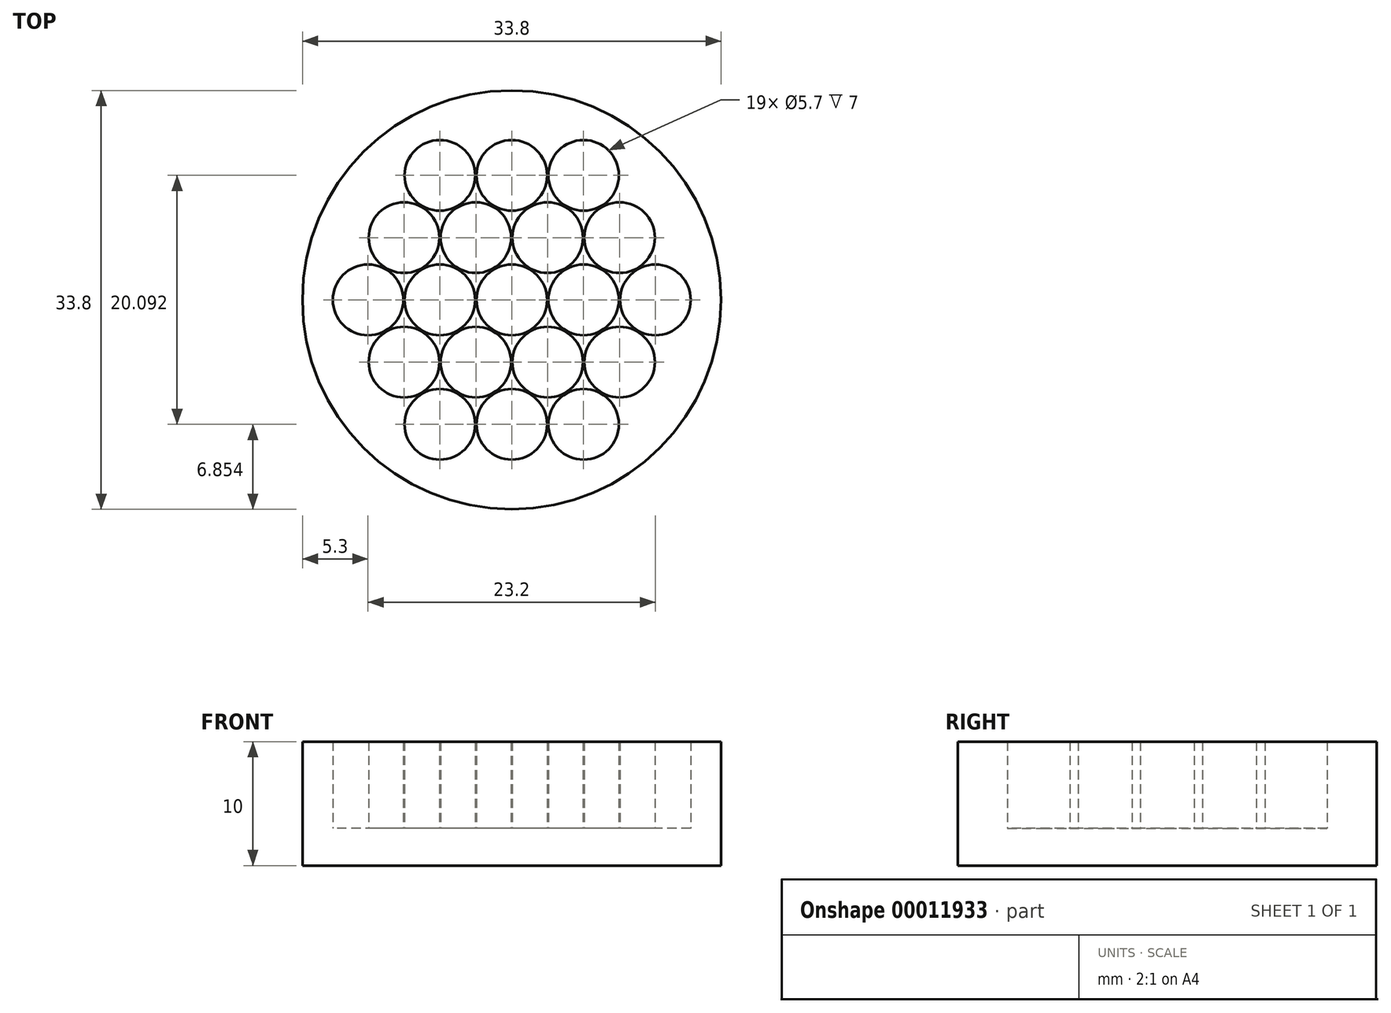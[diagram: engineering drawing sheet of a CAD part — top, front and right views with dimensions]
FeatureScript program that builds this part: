
annotation { "Feature Type Name" : "Feature", "Feature Type Description" : "" }
export const myFeature = defineFeature(function(context is Context, id is Id, definition is map)
    precondition{}
    {
        {
            var Q0;
            Q0=qCreatedBy(makeId("Top.planeOp"),FACE);
            var sketch = newSketch(context, id + "F0", { "sketchPlane" : qUnion([Q0])});
            skCircle(sketch, "E0", {"center": v(0, 0) * mm, "radius": 16.9 * mm});
            skLineSegment(sketch, "E1", {"start": v(-16.9, 0) * mm, "end": v(16.9, 0) * mm, "construction": true});
            skCircle(sketch, "E2.cCircle", {"center": v(0, 0) * mm, "radius": 16.9 * mm, "construction": true});
            skLineSegment(sketch, "E2.0", {"start": v(16.9, 0) * mm, "end": v(8.45, -14.64) * mm});
            skLineSegment(sketch, "E2.1", {"start": v(8.45, -14.64) * mm, "end": v(-8.45, -14.64) * mm});
            skLineSegment(sketch, "E2.2", {"start": v(-8.45, -14.64) * mm, "end": v(-16.9, 0) * mm});
            skLineSegment(sketch, "E2.3", {"start": v(-16.9, 0) * mm, "end": v(-8.45, 14.64) * mm});
            skLineSegment(sketch, "E2.4", {"start": v(-8.45, 14.64) * mm, "end": v(8.45, 14.64) * mm});
            skLineSegment(sketch, "E2.5", {"start": v(8.45, 14.64) * mm, "end": v(16.9, 0) * mm});
            skCircle(sketch, "E3", {"center": v(0, 0) * mm, "radius": 2.85 * mm});
            skCircle(sketch, "E4.1.0.0", {"center": v(5.8, 0) * mm, "radius": 2.85 * mm});
            skCircle(sketch, "E4.2.0.0", {"center": v(11.6, 0) * mm, "radius": 2.85 * mm});
            skLineSegment(sketch, "E4.direction1", {"start": v(0, 0) * mm, "end": v(5.8, 0) * mm, "construction": true});
            skCircle(sketch, "E5.1.0", {"center": v(2.9, 5.02) * mm, "radius": 2.85 * mm});
            skCircle(sketch, "E5.2.0", {"center": v(-2.9, 5.02) * mm, "radius": 2.85 * mm});
            skCircle(sketch, "E5.3.0", {"center": v(-5.8, 0) * mm, "radius": 2.85 * mm});
            skCircle(sketch, "E5.4.0", {"center": v(-2.9, -5.02) * mm, "radius": 2.85 * mm});
            skCircle(sketch, "E5.5.0", {"center": v(2.9, -5.02) * mm, "radius": 2.85 * mm});
            skCircle(sketch, "E6.1.0", {"center": v(5.8, 10.05) * mm, "radius": 2.85 * mm});
            skCircle(sketch, "E6.2.0", {"center": v(-5.8, 10.05) * mm, "radius": 2.85 * mm});
            skCircle(sketch, "E6.3.0", {"center": v(-11.6, 0) * mm, "radius": 2.85 * mm});
            skCircle(sketch, "E6.4.0", {"center": v(-5.8, -10.05) * mm, "radius": 2.85 * mm});
            skCircle(sketch, "E6.5.0", {"center": v(5.8, -10.05) * mm, "radius": 2.85 * mm});
            skLineSegment(sketch, "E7", {"start": v(5.8, -10.05) * mm, "end": v(11.6, 0) * mm, "construction": true});
            skCircle(sketch, "E8", {"center": v(8.7, -5.02) * mm, "radius": 2.85 * mm});
            skCircle(sketch, "E9.1.0", {"center": v(8.7, 5.02) * mm, "radius": 2.85 * mm});
            skCircle(sketch, "E9.2.0", {"center": v(0, 10.05) * mm, "radius": 2.85 * mm});
            skCircle(sketch, "E9.3.0", {"center": v(-8.7, 5.02) * mm, "radius": 2.85 * mm});
            skCircle(sketch, "E9.4.0", {"center": v(-8.7, -5.02) * mm, "radius": 2.85 * mm});
            skCircle(sketch, "E9.5.0", {"center": v(0, -10.05) * mm, "radius": 2.85 * mm});
            skSolve(sketch);
        }
        {
            var Q0;
            Q0 = qSketchRegion(id + "F0", true);
            extrude(context, id + "F1", {"entities" : qUnion([Q0]), "depth" : 7 * mm});
        }
        {
            var Q0;
            Q0=makeQuery(id+"F1.opExtrude","CAP_FACE",FACE,{"disambiguationData":[OSD([sQuery(id+"F0.wireOp",EDGE,"E0"),sQuery(id+"F0.wireOp",EDGE,"E3"),sQuery(id+"F0.wireOp",EDGE,"E4.1.0.0"),sQuery(id+"F0.wireOp",EDGE,"E4.2.0.0"),sQuery(id+"F0.wireOp",EDGE,"E5.1.0"),sQuery(id+"F0.wireOp",EDGE,"E5.2.0"),sQuery(id+"F0.wireOp",EDGE,"E5.3.0"),sQuery(id+"F0.wireOp",EDGE,"E5.4.0"),sQuery(id+"F0.wireOp",EDGE,"E5.5.0"),sQuery(id+"F0.wireOp",EDGE,"E6.1.0"),sQuery(id+"F0.wireOp",EDGE,"E6.2.0"),sQuery(id+"F0.wireOp",EDGE,"E6.3.0"),sQuery(id+"F0.wireOp",EDGE,"E6.4.0"),sQuery(id+"F0.wireOp",EDGE,"E6.5.0"),sQuery(id+"F0.wireOp",EDGE,"E8"),sQuery(id+"F0.wireOp",EDGE,"E9.1.0"),sQuery(id+"F0.wireOp",EDGE,"E9.2.0"),sQuery(id+"F0.wireOp",EDGE,"E9.3.0"),sQuery(id+"F0.wireOp",EDGE,"E9.4.0"),sQuery(id+"F0.wireOp",EDGE,"E9.5.0")])],"isStart":true});
            var sketch = newSketch(context, id + "F2", { "sketchPlane" : qUnion([Q0])});
            skCircle(sketch, "E10", {"center": v(0, 0) * mm, "radius": 16.9 * mm});
            skSolve(sketch);
        }
        {
            var Q0;
            Q0 = qSketchRegion(id + "F2", true);
            extrude(context, id + "F3", {"entities" : qUnion([Q0]), "operationType" : NewBodyOperationType.ADD, "depth" : 3 * mm});
        }
    });
